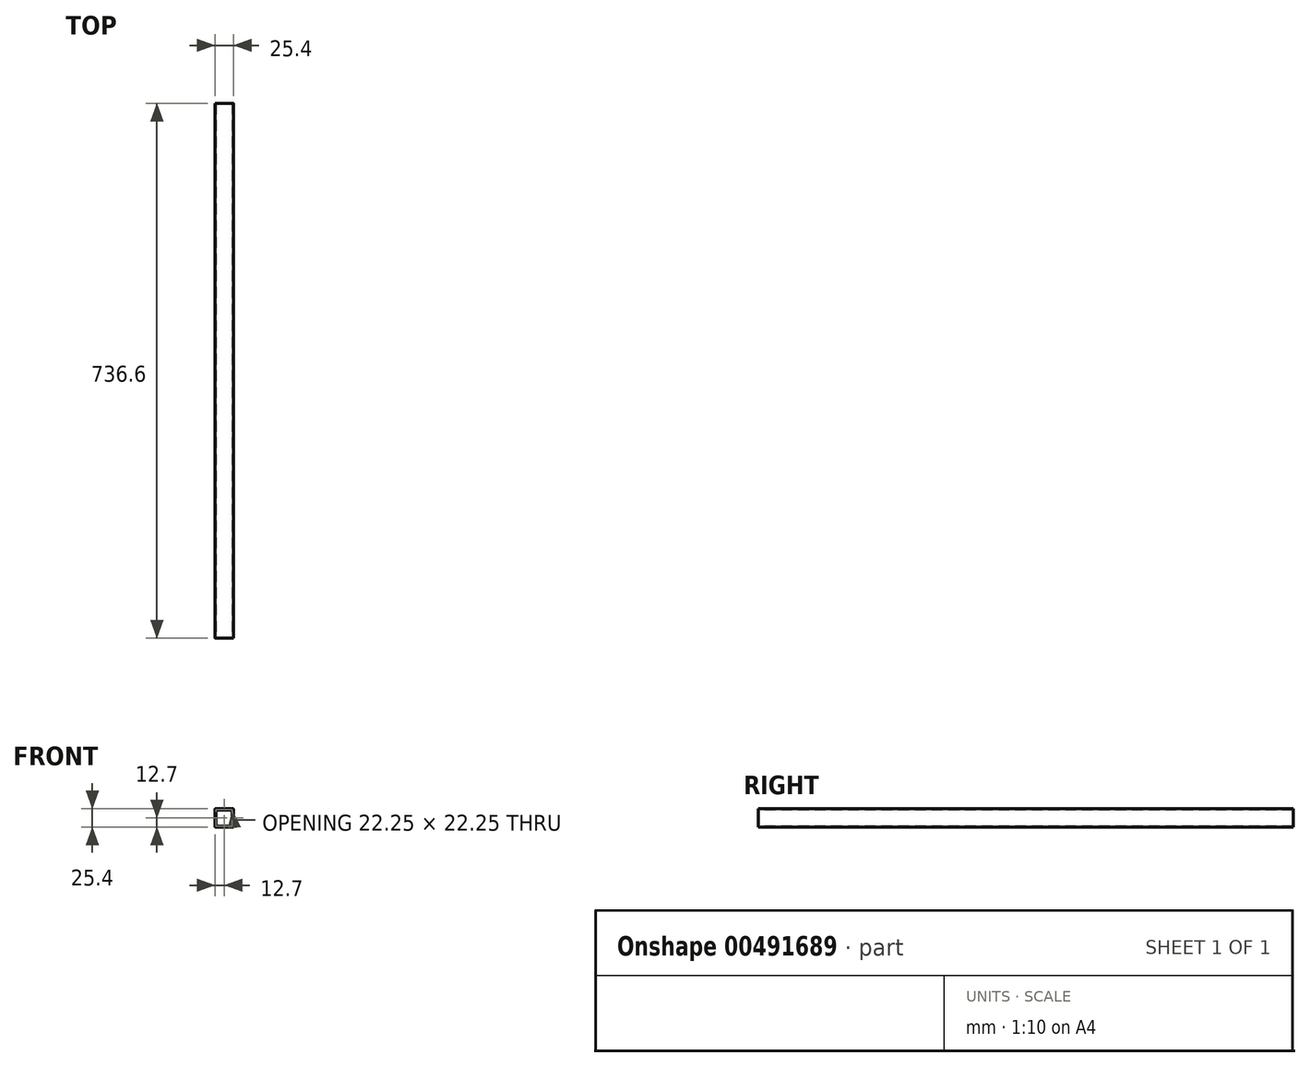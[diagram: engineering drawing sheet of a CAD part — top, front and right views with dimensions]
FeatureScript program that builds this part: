
annotation { "Feature Type Name" : "Feature", "Feature Type Description" : "" }
export const myFeature = defineFeature(function(context is Context, id is Id, definition is map)
    precondition{}
    {
        {
            var Q0;
            Q0=qCreatedBy(makeId("Front.planeOp"),FACE);
            var sketch = newSketch(context, id + "F0", { "sketchPlane" : qUnion([Q0])});
            skLineSegment(sketch, "E0.bottom", {"start": v(12.7, 12.7) * mm, "end": v(-12.7, 12.7) * mm});
            skLineSegment(sketch, "E0.top", {"start": v(12.7, -12.7) * mm, "end": v(-12.7, -12.7) * mm});
            skLineSegment(sketch, "E0.left", {"start": v(12.7, 12.7) * mm, "end": v(12.7, -12.7) * mm});
            skLineSegment(sketch, "E0.right", {"start": v(-12.7, 12.7) * mm, "end": v(-12.7, -12.7) * mm});
            skPoint(sketch, "E0.middle", {"position": v(0, 0) * mm});
            skSolve(sketch);
        }
        {
            var Q0;
            Q0 = qSketchRegion(id + "F0", true);
            extrude(context, id + "F1", {"entities" : qUnion([Q0]), "depth" : 736.6 * mm});
        }
        {
            var Q0;
            Q0=makeQuery(id+"F1.opExtrude","CAP_FACE",FACE,{"disambiguationData":[OSD([sQuery(id+"F0.wireOp",EDGE,"E0.bottom"),sQuery(id+"F0.wireOp",EDGE,"E0.top"),sQuery(id+"F0.wireOp",EDGE,"E0.left"),sQuery(id+"F0.wireOp",EDGE,"E0.right")])],"isStart":false});
            var sketch = newSketch(context, id + "F2", { "sketchPlane" : qUnion([Q0])});
            skLineSegment(sketch, "E1.bottom", {"start": v(-11.13, 11.13) * mm, "end": v(11.13, 11.13) * mm});
            skLineSegment(sketch, "E1.top", {"start": v(-11.13, -11.13) * mm, "end": v(11.13, -11.13) * mm});
            skLineSegment(sketch, "E1.left", {"start": v(-11.13, 11.13) * mm, "end": v(-11.13, -11.13) * mm});
            skLineSegment(sketch, "E1.right", {"start": v(11.13, 11.13) * mm, "end": v(11.13, -11.13) * mm});
            skPoint(sketch, "E1.middle", {"position": v(0, 0) * mm});
            skSolve(sketch);
        }
        {
            var Q0;
            Q0 = qSketchRegion(id + "F2", true);
            extrude(context, id + "F3", {"entities" : qUnion([Q0]), "operationType" : NewBodyOperationType.REMOVE, "endBound" : BoundingType.UP_TO_NEXT, "oppositeDirection" : true, "depth" : 25.4 * mm});
        }
        {
            var Q0;
            Q0=makeQuery(id+"F3.boolean.opBoolean","COPY",EDGE,{"derivedFrom":makeQuery(id+"F3.opExtrude","SWEPT_EDGE",EDGE,{"disambiguationData":[OSD([sQuery(id+"F2.wireOp",EDGE,"E1.bottom"),sQuery(id+"F2.wireOp",EDGE,"E1.left")])]})});
            var Q1;
            Q1=makeQuery(id+"F3.boolean.opBoolean","COPY",EDGE,{"derivedFrom":makeQuery(id+"F3.opExtrude","SWEPT_EDGE",EDGE,{"disambiguationData":[OSD([sQuery(id+"F2.wireOp",EDGE,"E1.top"),sQuery(id+"F2.wireOp",EDGE,"E1.right")])]})});
            var Q2;
            Q2=makeQuery(id+"F3.boolean.opBoolean","COPY",EDGE,{"derivedFrom":makeQuery(id+"F3.opExtrude","SWEPT_EDGE",EDGE,{"disambiguationData":[OSD([sQuery(id+"F2.wireOp",EDGE,"E1.bottom"),sQuery(id+"F2.wireOp",EDGE,"E1.right")])]})});
            var Q3;
            Q3=makeQuery(id+"F3.boolean.opBoolean","COPY",EDGE,{"derivedFrom":makeQuery(id+"F3.opExtrude","SWEPT_EDGE",EDGE,{"disambiguationData":[OSD([sQuery(id+"F2.wireOp",EDGE,"E1.top"),sQuery(id+"F2.wireOp",EDGE,"E1.left")])]})});
            fillet(context, id + "F4", {"entities" : qUnion([Q0, Q1, Q2, Q3]), "radius" : 1.52 * mm, "tangentPropagation" : true, "allowEdgeOverflow" : false});
        }
        {
            var Q0;
            Q0=makeQuery(id+"F1.opExtrude","SWEPT_EDGE",EDGE,{"disambiguationData":[OSD([sQuery(id+"F0.wireOp",EDGE,"E0.bottom"),sQuery(id+"F0.wireOp",EDGE,"E0.left")])]});
            var Q1;
            Q1=makeQuery(id+"F1.opExtrude","SWEPT_EDGE",EDGE,{"disambiguationData":[OSD([sQuery(id+"F0.wireOp",EDGE,"E0.top"),sQuery(id+"F0.wireOp",EDGE,"E0.left")])]});
            var Q2;
            Q2=makeQuery(id+"F1.opExtrude","SWEPT_EDGE",EDGE,{"disambiguationData":[OSD([sQuery(id+"F0.wireOp",EDGE,"E0.top"),sQuery(id+"F0.wireOp",EDGE,"E0.right")])]});
            var Q3;
            Q3=makeQuery(id+"F1.opExtrude","SWEPT_EDGE",EDGE,{"disambiguationData":[OSD([sQuery(id+"F0.wireOp",EDGE,"E0.bottom"),sQuery(id+"F0.wireOp",EDGE,"E0.right")])]});
            fillet(context, id + "F5", {"entities" : qUnion([Q0, Q1, Q2, Q3]), "radius" : 0.25 * mm, "tangentPropagation" : true, "allowEdgeOverflow" : false});
        }
    });
